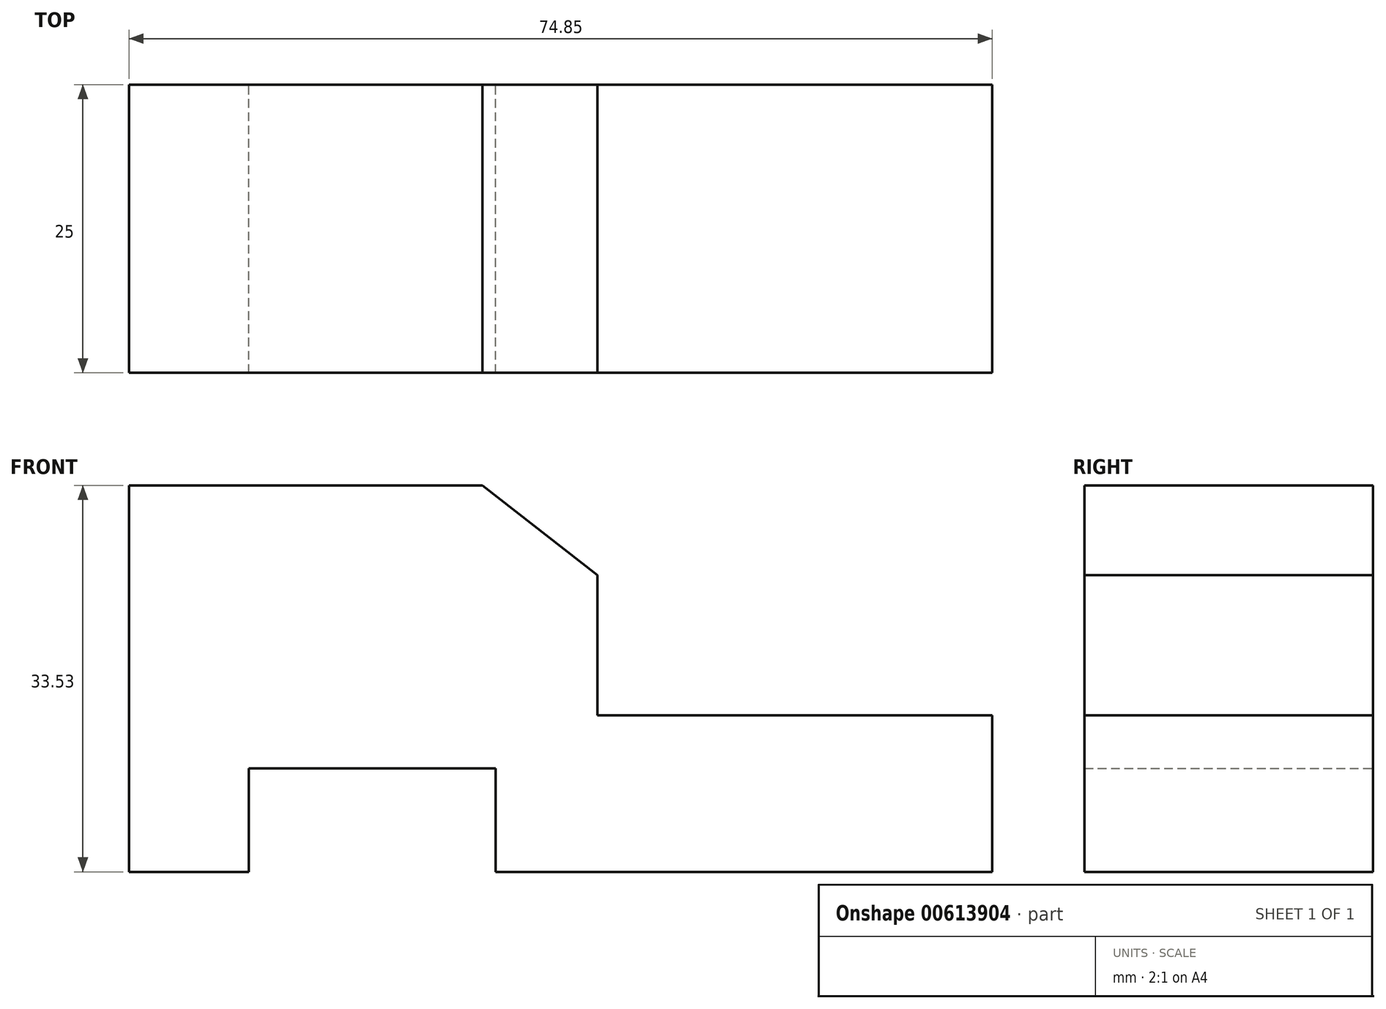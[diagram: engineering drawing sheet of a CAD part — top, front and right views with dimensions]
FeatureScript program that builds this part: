
annotation { "Feature Type Name" : "Feature", "Feature Type Description" : "" }
export const myFeature = defineFeature(function(context is Context, id is Id, definition is map)
    precondition{}
    {
        {
            var Q0;
            Q0=qCreatedBy(makeId("Front.planeOp"),FACE);
            var sketch = newSketch(context, id + "F0", { "sketchPlane" : qUnion([Q0])});
            skLineSegment(sketch, "E0", {"start": v(-40.6, 30.06) * mm, "end": v(-9.97, 30.06) * mm});
            skLineSegment(sketch, "E1", {"start": v(-9.97, 30.06) * mm, "end": v(0, 22.25) * mm});
            skLineSegment(sketch, "E2", {"start": v(0, 22.25) * mm, "end": v(0, 10.11) * mm});
            skLineSegment(sketch, "E3", {"start": v(0, 10.11) * mm, "end": v(34.25, 10.11) * mm});
            skLineSegment(sketch, "E4", {"start": v(34.25, 10.11) * mm, "end": v(34.25, -3.47) * mm});
            skLineSegment(sketch, "E5", {"start": v(34.25, -3.47) * mm, "end": v(-8.81, -3.47) * mm});
            skLineSegment(sketch, "E6", {"start": v(-8.81, -3.47) * mm, "end": v(-8.81, 5.5) * mm});
            skLineSegment(sketch, "E7", {"start": v(-8.81, 5.5) * mm, "end": v(-30.2, 5.5) * mm});
            skLineSegment(sketch, "E8", {"start": v(-30.2, 5.5) * mm, "end": v(-30.2, -3.47) * mm});
            skLineSegment(sketch, "E9", {"start": v(-30.2, -3.47) * mm, "end": v(-40.6, -3.47) * mm});
            skLineSegment(sketch, "E10", {"start": v(-40.6, -3.47) * mm, "end": v(-40.6, 30.06) * mm});
            skSolve(sketch);
        }
        {
            var Q0;
            Q0 = qSketchRegion(id + "F0", true);
            extrude(context, id + "F1", {"entities" : qUnion([Q0]), "depth" : 25 * mm, "offsetDistance" : 25 * mm});
        }
    });
